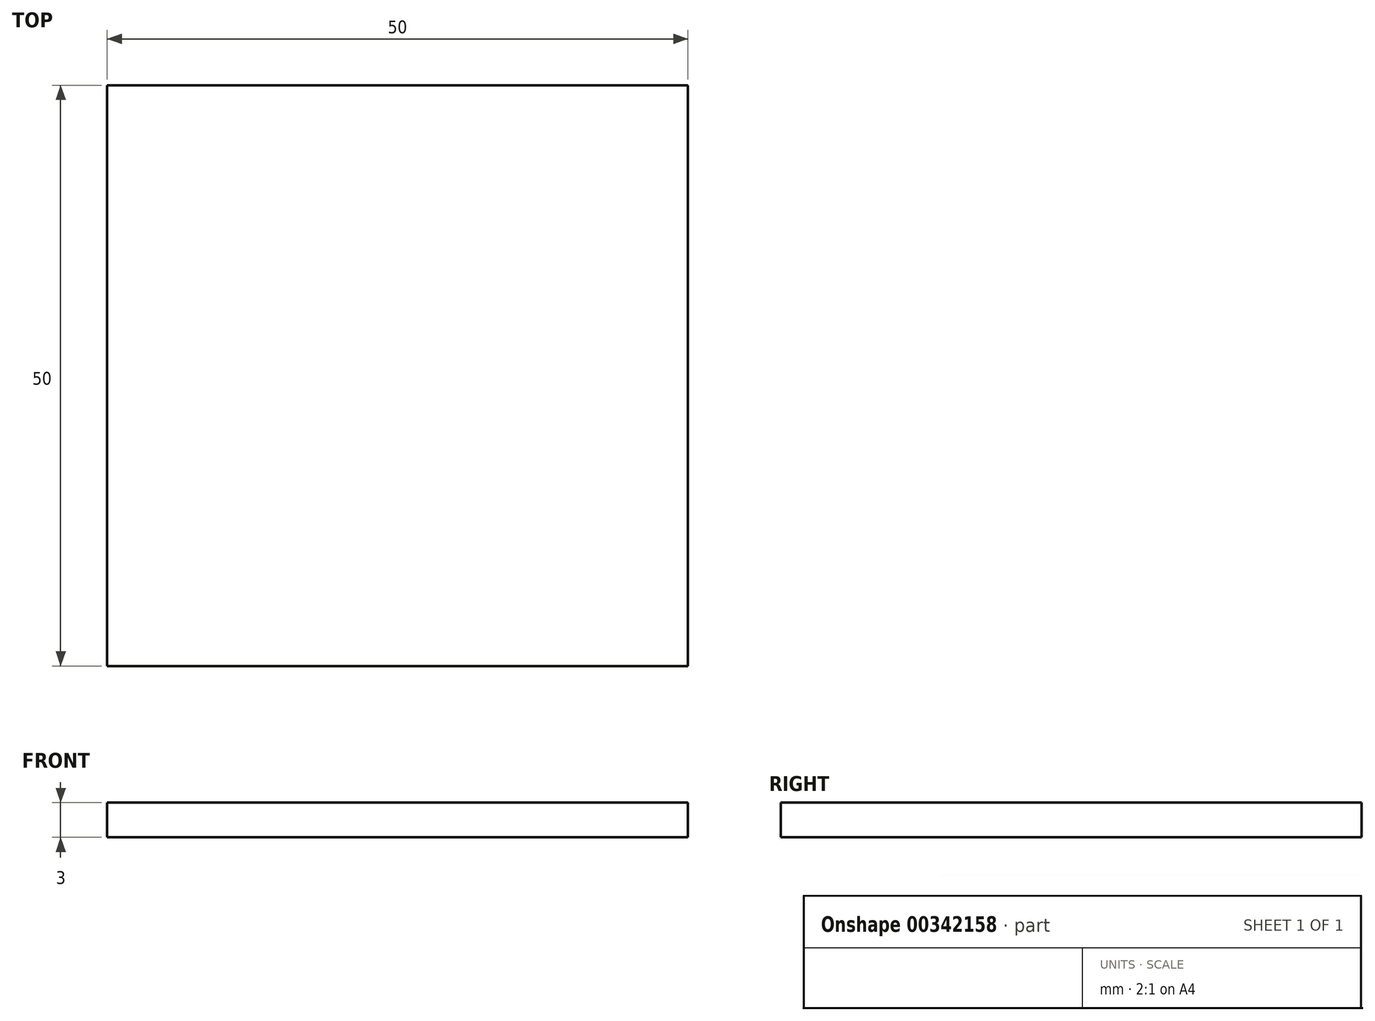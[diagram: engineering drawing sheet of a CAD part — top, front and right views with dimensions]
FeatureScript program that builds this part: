
annotation { "Feature Type Name" : "Feature", "Feature Type Description" : "" }
export const myFeature = defineFeature(function(context is Context, id is Id, definition is map)
    precondition{}
    {
        {
            var Q0;
            Q0=qCreatedBy(makeId("Top.planeOp"),FACE);
            var sketch = newSketch(context, id + "F0", { "sketchPlane" : qUnion([Q0])});
            skLineSegment(sketch, "E0.bottom", {"start": v(-25, 25) * mm, "end": v(25, 25) * mm});
            skLineSegment(sketch, "E0.top", {"start": v(-25, -25) * mm, "end": v(25, -25) * mm});
            skLineSegment(sketch, "E0.left", {"start": v(-25, 25) * mm, "end": v(-25, -25) * mm});
            skLineSegment(sketch, "E0.right", {"start": v(25, 25) * mm, "end": v(25, -25) * mm});
            skPoint(sketch, "E0.middle", {"position": v(0, 0) * mm});
            skSolve(sketch);
        }
        {
            var Q0;
            Q0=qSketchRegion(id+"F0",true);
            extrude(context, id + "F1", {"entities" : qUnion([Q0]), "endBound" : BoundingType.SYMMETRIC, "depth" : 3 * mm});
        }
    });
